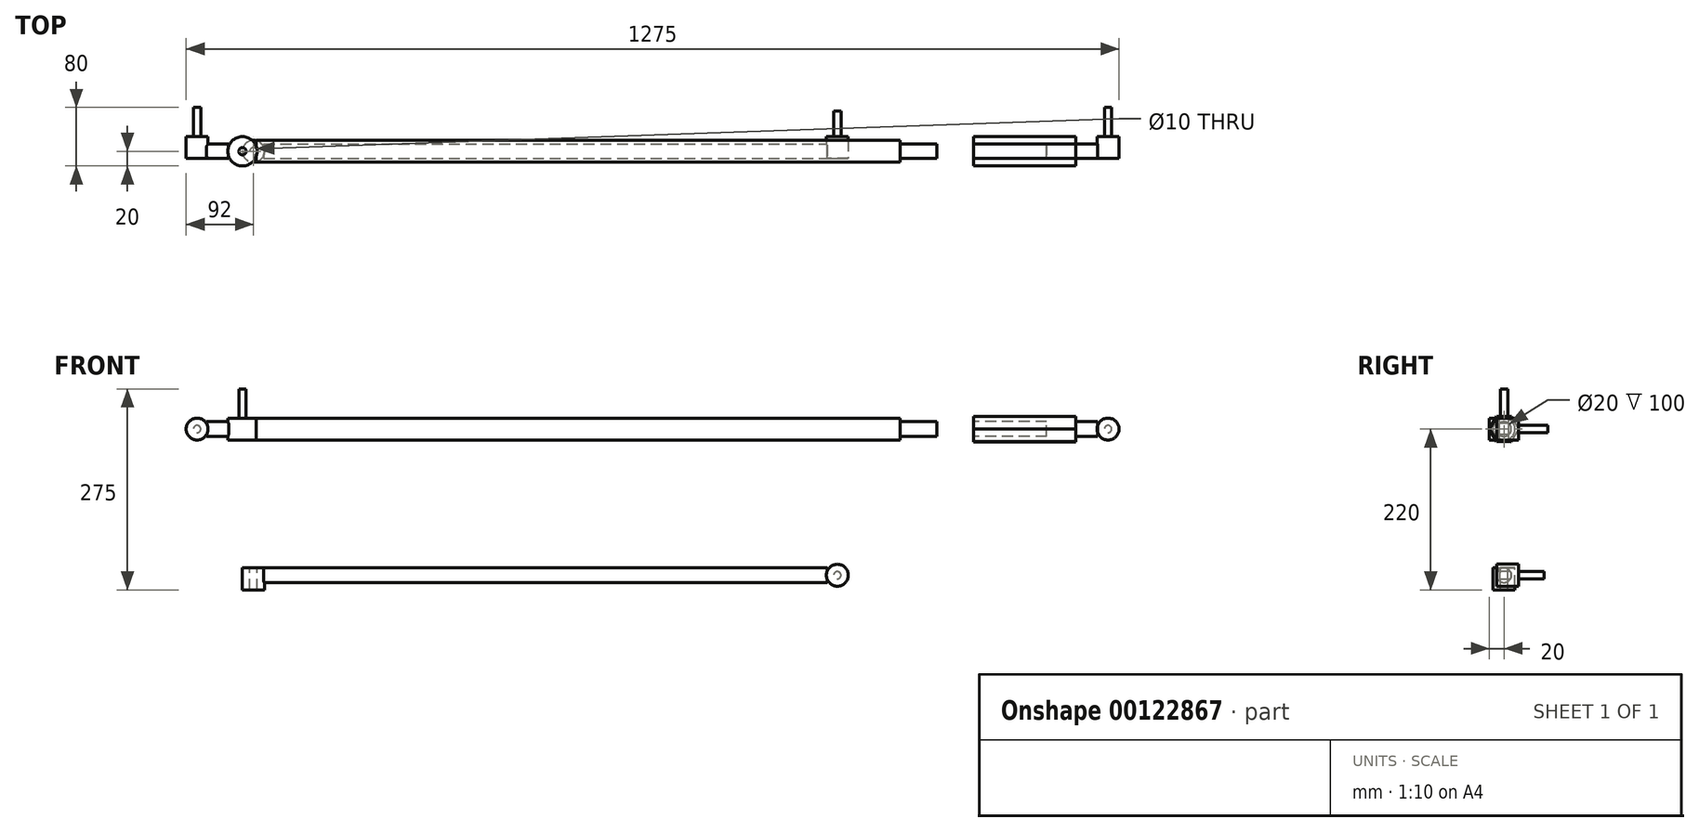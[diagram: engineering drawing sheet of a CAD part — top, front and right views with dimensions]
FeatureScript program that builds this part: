
annotation { "Feature Type Name" : "Feature", "Feature Type Description" : "" }
export const myFeature = defineFeature(function(context is Context, id is Id, definition is map)
    precondition{}
    {
        {
            var Q0;
            Q0=qCreatedBy(makeId("Right.planeOp"),FACE);
            var sketch = newSketch(context, id + "F0", { "sketchPlane" : qUnion([Q0])});
            skCircle(sketch, "E0", {"center": v(0, 0) * mm, "radius": 20 * mm});
            skCircle(sketch, "E1.cCircle", {"center": v(0, 0) * mm, "radius": 20 * mm, "construction": true});
            skLineSegment(sketch, "E1.0", {"start": v(10.09, 17.27) * mm, "end": v(20, -0.1) * mm});
            skLineSegment(sketch, "E1.1", {"start": v(20, -0.1) * mm, "end": v(9.91, -17.37) * mm});
            skLineSegment(sketch, "E1.2", {"start": v(9.91, -17.37) * mm, "end": v(-10.09, -17.27) * mm});
            skLineSegment(sketch, "E1.3", {"start": v(-10.09, -17.27) * mm, "end": v(-20, 0.1) * mm});
            skLineSegment(sketch, "E1.4", {"start": v(-20, 0.1) * mm, "end": v(-9.91, 17.37) * mm});
            skLineSegment(sketch, "E1.5", {"start": v(-9.91, 17.37) * mm, "end": v(10.09, 17.27) * mm});
            skCircle(sketch, "E2", {"center": v(0, 0) * mm, "radius": 10 * mm});
            skSolve(sketch);
        }
        {
            var Q0;
            Q0=makeQuery(id+"F0.imprint","IMPRINT",FACE,{"disambiguationData":[TD([[makeQuery(id+"F0.imprint","IMPRINT",EDGE,{"derivedFrom":sQuery(id+"F0.wireOp",EDGE,"E1.0")}),-1.0]])]});
            extrude(context, id + "F1", {"entities" : qUnion([Q0]), "depth" : 140 * mm});
        }
        {
            var Q0;
            Q0=qCreatedBy(makeId("Right.planeOp"),FACE);
            cPlane(context, id + "F2", {"entities" : qUnion([Q0]), "cplaneType" : CPlaneType.OFFSET, "offset" : 100 * mm, "width" : 150 * mm, "height" : 150 * mm});
        }
        {
            var Q0;
            Q0=qCreatedBy(id+"F2.planeOp",FACE);
            var sketch = newSketch(context, id + "F3", { "sketchPlane" : qUnion([Q0])});
            skCircle(sketch, "E3.0", {"center": v(0, 0) * mm, "radius": 10 * mm});
            skSolve(sketch);
        }
        {
            var Q0;
            Q0=qSketchRegion(id+"F3",true);
            extrude(context, id + "F4", {"entities" : qUnion([Q0]), "operationType" : NewBodyOperationType.ADD, "depth" : 70 * mm});
        }
        {
            var Q0;
            Q0=qCreatedBy(makeId("Front.planeOp"),FACE);
            cPlane(context, id + "F5", {"entities" : qUnion([Q0]), "cplaneType" : CPlaneType.OFFSET, "offset" : 10 * mm, "width" : 150 * mm, "height" : 150 * mm});
        }
        {
            var Q0;
            Q0=qCreatedBy(id+"F5.planeOp",FACE);
            var sketch = newSketch(context, id + "F6", { "sketchPlane" : qUnion([Q0])});
            skLineSegment(sketch, "E4", {"start": v(0, 0) * mm, "end": v(184, 0) * mm});
            skCircle(sketch, "E5", {"center": v(184, 0) * mm, "radius": 15 * mm});
            skSolve(sketch);
        }
        {
            var Q0;
            Q0=qSketchRegion(id+"F6",true);
            extrude(context, id + "F7", {"entities" : qUnion([Q0]), "oppositeDirection" : true, "depth" : 30 * mm});
        }
        {
            var Q0;
            Q0=qCreatedBy(makeId("Front.planeOp"),FACE);
            var sketch = newSketch(context, id + "F8", { "sketchPlane" : qUnion([Q0])});
            skLineSegment(sketch, "E6", {"start": v(0, 0) * mm, "end": v(184, 0) * mm});
            skCircle(sketch, "E7", {"center": v(184, 0) * mm, "radius": 5 * mm});
            skSolve(sketch);
        }
        {
            var Q0;
            Q0 = qSketchRegion(id + "F8", true);
            extrude(context, id + "F9", {"entities" : qUnion([Q0]), "operationType" : NewBodyOperationType.ADD, "oppositeDirection" : true, "depth" : 60 * mm});
        }
        {
            var Q0;
            Q0=qCreatedBy(makeId("Front.planeOp"),FACE);
            var sketch = newSketch(context, id + "F10", { "sketchPlane" : qUnion([Q0])});
            skLineSegment(sketch, "E8", {"start": v(-50, 0) * mm, "end": v(-980, 0) * mm});
            skLineSegment(sketch, "E9", {"start": v(-50, 0) * mm, "end": v(-50, 10) * mm});
            skLineSegment(sketch, "E10", {"start": v(-50, 10) * mm, "end": v(-100, 10) * mm});
            skLineSegment(sketch, "E11", {"start": v(-100, 10) * mm, "end": v(-100, 15) * mm});
            skLineSegment(sketch, "E12", {"start": v(-100, 15) * mm, "end": v(-980, 15) * mm});
            skLineSegment(sketch, "E13", {"start": v(-980, 15) * mm, "end": v(-980, 0) * mm});
            skSolve(sketch);
        }
        {
            var Q0;
            Q0=makeQuery(id+"F10.imprint","IMPRINT",FACE,{"disambiguationData":[TD([[makeQuery(id+"F10.imprint","IMPRINT",EDGE,{"derivedFrom":sQuery(id+"F10.wireOp",EDGE,"E8")}),-1.0]])]});
            var Q1;
            Q1=sQuery(id+"F10.wireOp",EDGE,"E8");
            revolve(context, id + "F11", {"entities" : qUnion([Q0]), "axis" : qUnion([Q1]), "revolveType" : RevolveType.FULL});
        }
        {
            var Q0;
            Q0=qCreatedBy(makeId("Top.planeOp"),FACE);
            cPlane(context, id + "F12", {"entities" : qUnion([Q0]), "cplaneType" : CPlaneType.OFFSET, "offset" : 15 * mm, "width" : 150 * mm, "height" : 150 * mm});
        }
        {
            var Q0;
            Q0=qCreatedBy(id+"F12.planeOp",FACE);
            var sketch = newSketch(context, id + "F13", { "sketchPlane" : qUnion([Q0])});
            skLineSegment(sketch, "E14", {"start": v(0, 0) * mm, "end": v(-999, 0) * mm});
            skCircle(sketch, "E15", {"center": v(-999, 0) * mm, "radius": 20 * mm});
            skSolve(sketch);
        }
        {
            var Q0;
            Q0 = qSketchRegion(id + "F13", true);
            extrude(context, id + "F14", {"entities" : qUnion([Q0]), "operationType" : NewBodyOperationType.ADD, "oppositeDirection" : true, "depth" : 30 * mm});
        }
        {
            var Q0;
            Q0=qCreatedBy(makeId("Top.planeOp"),FACE);
            var sketch = newSketch(context, id + "F15", { "sketchPlane" : qUnion([Q0])});
            skLineSegment(sketch, "E16", {"start": v(0, 0) * mm, "end": v(-999, 0) * mm});
            skCircle(sketch, "E17", {"center": v(-999, 0) * mm, "radius": 5 * mm});
            skSolve(sketch);
        }
        {
            var Q0;
            Q0 = qSketchRegion(id + "F15", true);
            extrude(context, id + "F16", {"entities" : qUnion([Q0]), "operationType" : NewBodyOperationType.ADD, "depth" : 55 * mm});
        }
        {
            var Q0;
            Q0=qCreatedBy(makeId("Top.planeOp"),FACE);
            var sketch = newSketch(context, id + "F17", { "sketchPlane" : qUnion([Q0])});
            skLineSegment(sketch, "E18", {"start": v(0, 0) * mm, "end": v(-1018, 0) * mm});
            skLineSegment(sketch, "E19", {"start": v(-1018, 0) * mm, "end": v(-1048, 0) * mm});
            skLineSegment(sketch, "E20", {"start": v(-1048, 0) * mm, "end": v(-1048, 10) * mm});
            skLineSegment(sketch, "E21", {"start": v(-1048, 10) * mm, "end": v(-1018, 10) * mm});
            skLineSegment(sketch, "E22", {"start": v(-1018, 10) * mm, "end": v(-1018, 0) * mm});
            skSolve(sketch);
        }
        {
            var Q0;
            Q0 = qSketchRegion(id + "F17", true);
            var Q1;
            Q1=sQuery(id+"F17.wireOp",EDGE,"E19");
            revolve(context, id + "F18", {"operationType" : NewBodyOperationType.ADD, "entities" : qUnion([Q0]), "axis" : qUnion([Q1]), "revolveType" : RevolveType.FULL});
        }
        {
            var Q0;
            Q0=qCreatedBy(id+"F5.planeOp",FACE);
            var sketch = newSketch(context, id + "F19", { "sketchPlane" : qUnion([Q0])});
            skLineSegment(sketch, "E23", {"start": v(0, 0) * mm, "end": v(-1061, 0) * mm});
            skCircle(sketch, "E24", {"center": v(-1061, 0) * mm, "radius": 15 * mm});
            skSolve(sketch);
        }
        {
            var Q0;
            Q0 = qSketchRegion(id + "F19", true);
            extrude(context, id + "F20", {"entities" : qUnion([Q0]), "operationType" : NewBodyOperationType.ADD, "oppositeDirection" : true, "depth" : 30 * mm});
        }
        {
            var Q0;
            Q0=qCreatedBy(makeId("Front.planeOp"),FACE);
            var sketch = newSketch(context, id + "F21", { "sketchPlane" : qUnion([Q0])});
            skLineSegment(sketch, "E25", {"start": v(0, 0) * mm, "end": v(-1061, 0) * mm});
            skCircle(sketch, "E26", {"center": v(-1061, 0) * mm, "radius": 5 * mm});
            skSolve(sketch);
        }
        {
            var Q0;
            Q0 = qSketchRegion(id + "F21", true);
            extrude(context, id + "F22", {"entities" : qUnion([Q0]), "operationType" : NewBodyOperationType.ADD, "oppositeDirection" : true, "depth" : 60 * mm});
        }
        {
            var Q0;
            Q0=qCreatedBy(makeId("Front.planeOp"),FACE);
            var sketch = newSketch(context, id + "F23", { "sketchPlane" : qUnion([Q0])});
            skLineSegment(sketch, "E27", {"start": v(0, 0) * mm, "end": v(0, -200) * mm});
            skLineSegment(sketch, "E28", {"start": v(0, -200) * mm, "end": v(-200, -200) * mm});
            skLineSegment(sketch, "E29", {"start": v(-200, -200) * mm, "end": v(-970, -200) * mm});
            skLineSegment(sketch, "E30", {"start": v(-970, -200) * mm, "end": v(-970, -190) * mm});
            skLineSegment(sketch, "E31", {"start": v(-970, -190) * mm, "end": v(-200, -190) * mm});
            skLineSegment(sketch, "E32", {"start": v(-200, -190) * mm, "end": v(-200, -200) * mm});
            skSolve(sketch);
        }
        {
            var Q0;
            Q0 = qSketchRegion(id + "F23", true);
            var Q1;
            Q1=sQuery(id+"F23.wireOp",EDGE,"E29");
            revolve(context, id + "F24", {"entities" : qUnion([Q0]), "axis" : qUnion([Q1]), "revolveType" : RevolveType.FULL});
        }
        {
            var Q0;
            Q0=qCreatedBy(id+"F5.planeOp",FACE);
            var sketch = newSketch(context, id + "F25", { "sketchPlane" : qUnion([Q0])});
            skLineSegment(sketch, "E33", {"start": v(0, 0) * mm, "end": v(0, -200) * mm});
            skLineSegment(sketch, "E34", {"start": v(0, -200) * mm, "end": v(-186, -200) * mm});
            skCircle(sketch, "E35", {"center": v(-186, -200) * mm, "radius": 15 * mm});
            skSolve(sketch);
        }
        {
            var Q0;
            Q0 = qSketchRegion(id + "F25", true);
            extrude(context, id + "F26", {"entities" : qUnion([Q0]), "operationType" : NewBodyOperationType.ADD, "oppositeDirection" : true, "depth" : 30 * mm});
        }
        {
            var Q0;
            Q0=qCreatedBy(makeId("Front.planeOp"),FACE);
            var sketch = newSketch(context, id + "F27", { "sketchPlane" : qUnion([Q0])});
            skLineSegment(sketch, "E36", {"start": v(0, 0) * mm, "end": v(0, -200) * mm});
            skLineSegment(sketch, "E37", {"start": v(0, -200) * mm, "end": v(-186, -200) * mm});
            skCircle(sketch, "E38", {"center": v(-186, -200) * mm, "radius": 5 * mm});
            skSolve(sketch);
        }
        {
            var Q0;
            Q0 = qSketchRegion(id + "F27", true);
            extrude(context, id + "F28", {"entities" : qUnion([Q0]), "operationType" : NewBodyOperationType.ADD, "oppositeDirection" : true, "depth" : 55 * mm});
        }
        {
            var Q0;
            Q0=qCreatedBy(makeId("Top.planeOp"),FACE);
            cPlane(context, id + "F29", {"entities" : qUnion([Q0]), "cplaneType" : CPlaneType.OFFSET, "offset" : 190 * mm, "oppositeDirection" : true, "width" : 150 * mm, "height" : 150 * mm});
        }
        {
            var Q0;
            Q0=qCreatedBy(id+"F29.planeOp",FACE);
            var sketch = newSketch(context, id + "F30", { "sketchPlane" : qUnion([Q0])});
            skLineSegment(sketch, "E39", {"start": v(0, 0) * mm, "end": v(-984, 0) * mm});
            skCircle(sketch, "E40", {"center": v(-984, 0) * mm, "radius": 15 * mm});
            skCircle(sketch, "E41", {"center": v(-984, 0) * mm, "radius": 5 * mm});
            skSolve(sketch);
        }
        {
            var Q0;
            Q0 = qSketchRegion(id + "F30", true);
            extrude(context, id + "F31", {"entities" : qUnion([Q0]), "operationType" : NewBodyOperationType.ADD, "oppositeDirection" : true, "depth" : 30 * mm});
        }
    });
